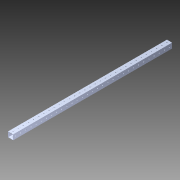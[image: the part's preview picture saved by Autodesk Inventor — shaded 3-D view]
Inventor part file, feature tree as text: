
AUTODESK INVENTOR PART (.ipt)
format: ipt  version: 2014 SP1 (Build 180222100, 222)  size: 1,278,464 bytes
history: native  units: in
note: dims shown in document units (in); Inventor stores cm internally (conversion verified against a paired STEP export)
features: pattern_circular x1, other x1, extrude x1, imported_body x1, sketch x1
ambient origin geometry x8: Origin, YZ Plane, XZ Plane, XY Plane, X Axis, Y Axis, Z Axis, Center Point
bodies: Body1 (feature_tree)
feature tree (5):
  pattern_circular  "CirPattern2"
  other  "1x1 tube1"
  extrude  "Extrusion1"  [1 undecoded]
  imported_body  "Base1"
  sketch  "Sketch1"  dims[d0=28.0in d1=0.0in]
note: 1 required parameter value undecoded (feature->parameter linkage not recoverable at this tier; creation-order binding heuristic only, values carry confidence <= 0.55)
